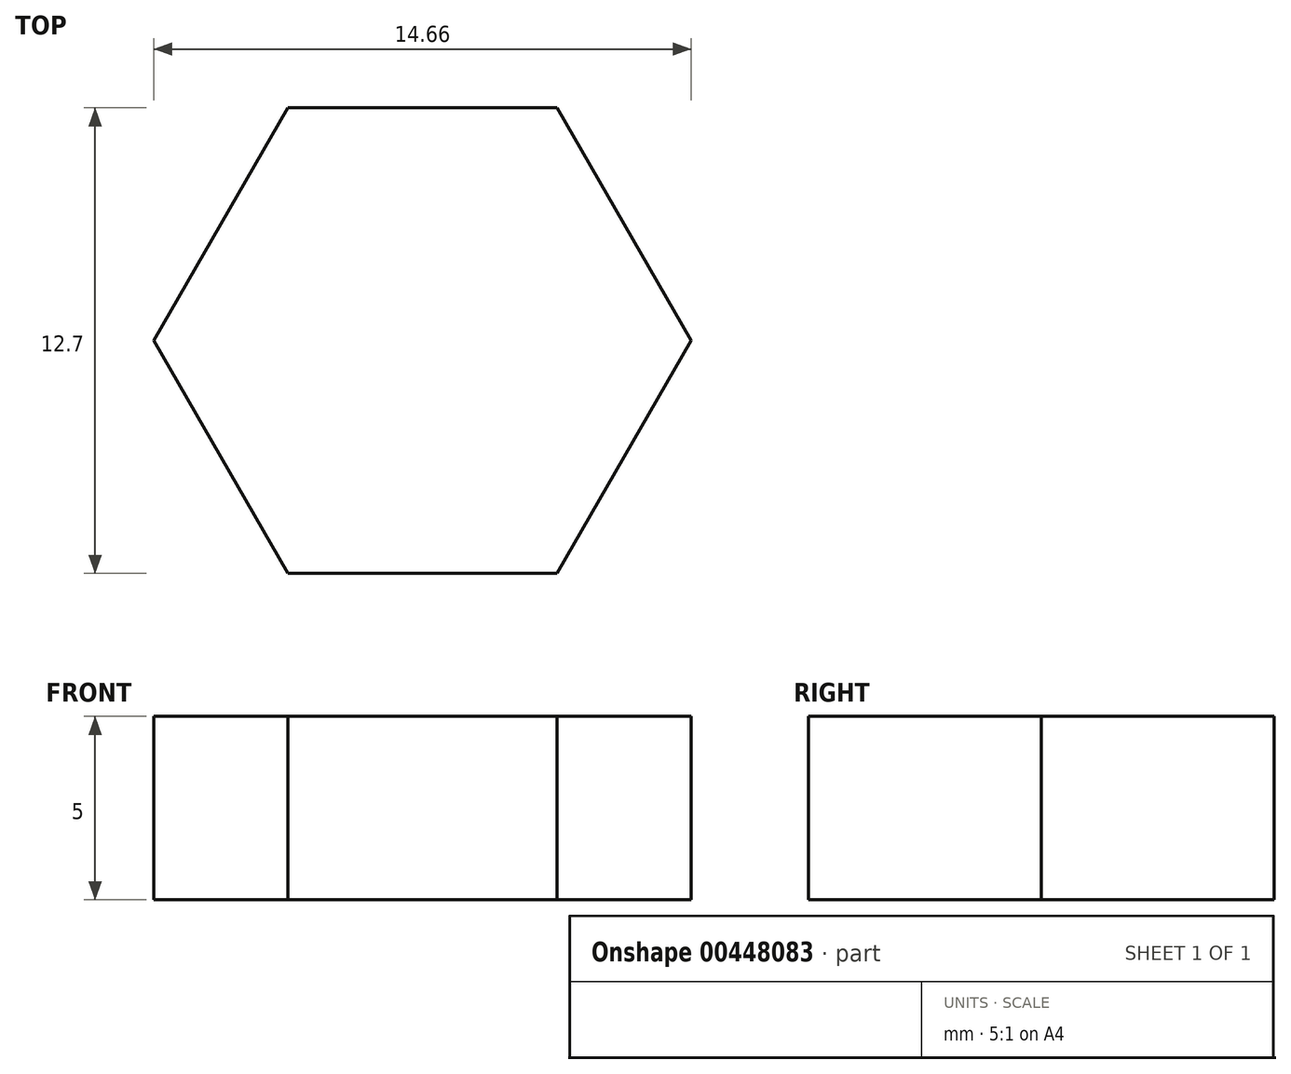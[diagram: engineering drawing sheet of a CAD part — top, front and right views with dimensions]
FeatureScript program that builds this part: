
annotation { "Feature Type Name" : "Feature", "Feature Type Description" : "" }
export const myFeature = defineFeature(function(context is Context, id is Id, definition is map)
    precondition{}
    {
        {
            assignVariable(context, id + "F0", {"name" : "ShaftL", "anyValue" : 5});
        }
        {
            var Q0;
            Q0=qCreatedBy(makeId("Top.planeOp"),FACE);
            var sketch = newSketch(context, id + "F1", { "sketchPlane" : qUnion([Q0])});
            skCircle(sketch, "E0.cCircle", {"center": v(0, 0) * mm, "radius": 6.35 * mm, "construction": true});
            skLineSegment(sketch, "E0.0", {"start": v(-3.67, 6.35) * mm, "end": v(3.67, 6.35) * mm});
            skLineSegment(sketch, "E0.1", {"start": v(3.67, 6.35) * mm, "end": v(7.33, 0) * mm});
            skLineSegment(sketch, "E0.2", {"start": v(7.33, 0) * mm, "end": v(3.67, -6.35) * mm});
            skLineSegment(sketch, "E0.3", {"start": v(3.67, -6.35) * mm, "end": v(-3.67, -6.35) * mm});
            skLineSegment(sketch, "E0.4", {"start": v(-3.67, -6.35) * mm, "end": v(-7.33, 0) * mm});
            skLineSegment(sketch, "E0.5", {"start": v(-7.33, 0) * mm, "end": v(-3.67, 6.35) * mm});
            skPoint(sketch, "E0.0.midPoint", {"position": v(0, 6.35) * mm});
            skSolve(sketch);
        }
        {
            var Q0;
            Q0 = qSketchRegion(id + "F1", true);
            extrude(context, id + "F2", {"entities" : qUnion([Q0]), "depth" : (getVariable(context, 'ShaftL')) * mm});
        }
    });
